# Revit family: Урна уличная круглая «Палермо»
name_source: partatom
category: Антураж
revit_build: Autodesk Revit 2017 (Build: 20160225_1515(x64)
units: mm (PartAtom-declared; Revit-internal decimal feet)

## family parameters
Всегда вертикально = Да
Источник визуального образа = Геометрия семейства
На основе рабочей плоскости = Нет
Общий = Нет
При загрузке вырезать с полостями = Нет
Точка расчета площади = Нет

## types (2) — shared parameters
ADSK_Вес = 20.00 кг
ADSK_Материал ведра = <По категории>
ADSK_Материал ламелей = <По категории>
ADSK_Материал урны = <По категории>
ADSK_Объем = 40 м³
ADSK_Размер_Высота = 765 мм
ADSK_Размер_Глубина = 400 мм
ADSK_Размер_Ширина = 440 мм
URL = https://hobbyka.ru
zero-valued in all types: Высота

## per-type parameters (varying)
| type | ADSK_Код изделия | ADSK_Наименование | Изготовитель | Стоимость |
| Урна уличная круглая «Палермо натур» |  |  | Хоббика | 18360 $ |
| Урна уличная круглая «Палермо» | 9676 | Урна уличная круглая «Палермо» | ООО "Хоббика" | 20088 $ |
